# Revit family: HVAC_Fireplaces_Regency-Fireplace_Plateau-Outdoor-Gas-Fireplace_PTO100
name_source: partatom
category: Specialty Equipment
units: mm (PartAtom-declared; Revit-internal decimal feet)

## family parameters
Classification Number = 23.40.20.34.14
Cut with Voids When Loaded = No
Enable Cutting in Views = No
Host = Face
Maintain Annotation Orientation = No
Part Type = Normal
Room Calculation Point = No
Round Connector Dimension = Use Diameter
Shared = No

## types (2) — shared parameters
Apparent Load = 0 VA
Current = 2 A
Default Elevation = 48 "
Depth = 11 "
Description = Fire pits and fireplaces can add dramatic, architectural focal points to your outdoor living space, but also the functional elements of providing both heat and light. This impressive linear 50-inch burner can be installed into a custom application that any landscape designer or homeowner can imagine.
Frequency = 60 Hz
Gas flow = 0.0 L/s
Height = 10 "
Housing Material = Regency Fireplace - Metal - Black
Manufacturer = Regency Fireplace
Number of Poles = 1
Orifce Size -Altitude 0-4500 ft = # 11 DMS
Pipe Diameter = 1 "
Power Consumption = 0 W
Power Factor = 1
Product Documentation Link = https://assets.regency-fire.com
Product Page URL = https://www.regency-fire.com
Product data url = https://www.bimobject.com
URL = https://www.regency-fire.com
Voltage = 120 V
Width = 106 "
zero-valued in all types: Version

## per-type parameters (varying)
| type | Fuel Type | Gas Connector Description | Manifold Pressure - High | Manifold Pressure - Low | Maximum Input Altitude 0-4500 ft. (0-1372m) | Minimum Input Altitude 0-4500 ft. (0-1372m) | Minimum Supply Pressure |
| PTO100-NG11 | Natural Gas | Natural gas supply | 7” W.C. (1.74 kPa) | 3.2” W.C. (0.80 kPa) | 128,000 Btu/h (37.52 kW) | 84,000 Btu/h (24.62 kW) | 10” W.C. (2.5 kPa) |
| PTO100-LP11 | Propane | Propane gas supply | 20” W.C. (4.98 kPa) | 12.8” W.C. (3.18 kPa) | 124,000 Btu/h (36.34 kW) | 148,000 Btu/h (28.72 kW) | 22” W.C. (5.46 kPa) |

note: column(s) folded — value = type name in every type: Model

## geometry (parser evidence)
native form markers: Sweep x5
no freeform markers — native parametric forms only
